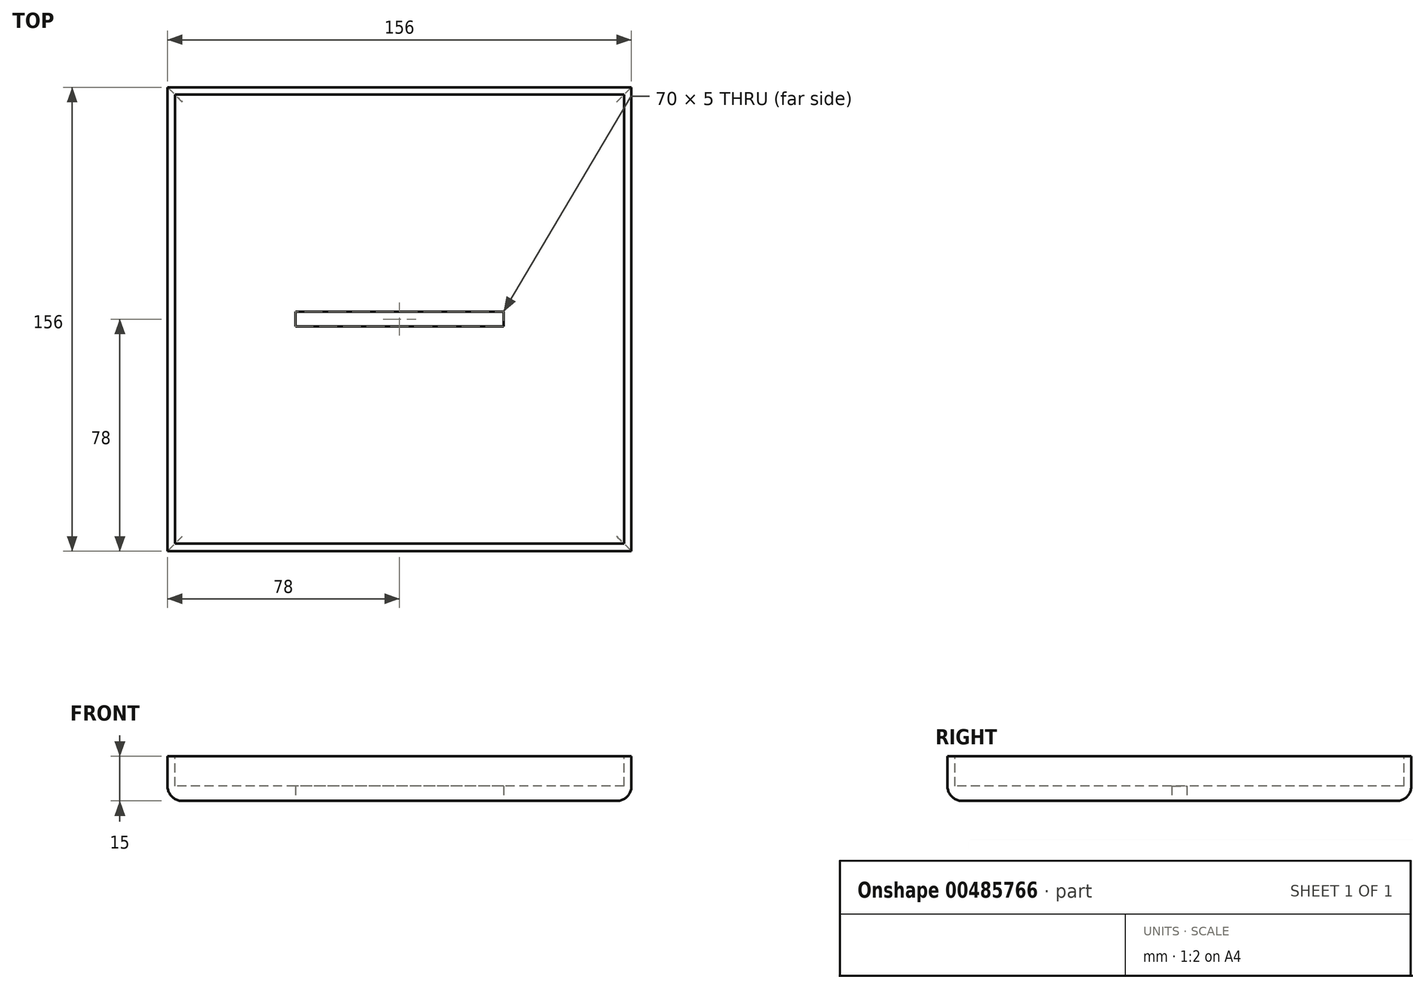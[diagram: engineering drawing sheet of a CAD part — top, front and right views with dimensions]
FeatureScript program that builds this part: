
annotation { "Feature Type Name" : "Feature", "Feature Type Description" : "" }
export const myFeature = defineFeature(function(context is Context, id is Id, definition is map)
    precondition{}
    {
        {
            var Q0;
            Q0=qCreatedBy(makeId("Top.planeOp"),FACE);
            var sketch = newSketch(context, id + "F0", { "sketchPlane" : qUnion([Q0])});
            skLineSegment(sketch, "E0.bottom", {"start": v(78, -78) * mm, "end": v(-78, -78) * mm});
            skLineSegment(sketch, "E0.top", {"start": v(78, 78) * mm, "end": v(-78, 78) * mm});
            skLineSegment(sketch, "E0.left", {"start": v(78, -78) * mm, "end": v(78, 78) * mm});
            skLineSegment(sketch, "E0.right", {"start": v(-78, -78) * mm, "end": v(-78, 78) * mm});
            skPoint(sketch, "E0.middle", {"position": v(0, 0) * mm});
            skSolve(sketch);
        }
        {
            var Q0;
            Q0 = qSketchRegion(id + "F0", true);
            extrude(context, id + "F1", {"entities" : qUnion([Q0]), "depth" : 15 * mm});
        }
        {
            var Q0;
            Q0=makeQuery(id+"F1.opExtrude","CAP_FACE",FACE,{"disambiguationData":[OSD([sQuery(id+"F0.wireOp",EDGE,"E0.bottom"),sQuery(id+"F0.wireOp",EDGE,"E0.top"),sQuery(id+"F0.wireOp",EDGE,"E0.left"),sQuery(id+"F0.wireOp",EDGE,"E0.right")])],"isStart":false});
            var sketch = newSketch(context, id + "F2", { "sketchPlane" : qUnion([Q0])});
            skLineSegment(sketch, "E1.bottom", {"start": v(75.5, 75.5) * mm, "end": v(-75.5, 75.5) * mm});
            skLineSegment(sketch, "E1.top", {"start": v(75.5, -75.5) * mm, "end": v(-75.5, -75.5) * mm});
            skLineSegment(sketch, "E1.left", {"start": v(75.5, 75.5) * mm, "end": v(75.5, -75.5) * mm});
            skLineSegment(sketch, "E1.right", {"start": v(-75.5, 75.5) * mm, "end": v(-75.5, -75.5) * mm});
            skPoint(sketch, "E1.middle", {"position": v(0, 0) * mm});
            skSolve(sketch);
        }
        {
            var Q0;
            Q0=makeQuery(id+"F2.imprint","IMPRINT",FACE,{"disambiguationData":[TD([[makeQuery(id+"F2.imprint","IMPRINT",EDGE,{"derivedFrom":sQuery(id+"F2.wireOp",EDGE,"E1.bottom")}),1.0]])]});
            extrude(context, id + "F3", {"entities" : qUnion([Q0]), "operationType" : NewBodyOperationType.REMOVE, "oppositeDirection" : true, "depth" : 10 * mm});
        }
        {
            var Q0;
            Q0=makeQuery(id+"F1.opExtrude","CAP_EDGE",EDGE,{"disambiguationData":[OSD([sQuery(id+"F0.wireOp",EDGE,"E0.left")])],"isStart":true});
            var Q1;
            Q1=makeQuery(id+"F1.opExtrude","CAP_EDGE",EDGE,{"disambiguationData":[OSD([sQuery(id+"F0.wireOp",EDGE,"E0.bottom")])],"isStart":true});
            var Q2;
            Q2=makeQuery(id+"F1.opExtrude","CAP_EDGE",EDGE,{"disambiguationData":[OSD([sQuery(id+"F0.wireOp",EDGE,"E0.right")])],"isStart":true});
            var Q3;
            Q3=makeQuery(id+"F1.opExtrude","CAP_EDGE",EDGE,{"disambiguationData":[OSD([sQuery(id+"F0.wireOp",EDGE,"E0.top")])],"isStart":true});
            fillet(context, id + "F4", {"entities" : qUnion([Q0, Q1, Q2, Q3]), "radius" : 5 * mm, "tangentPropagation" : true, "allowEdgeOverflow" : false});
        }
        {
            var Q0;
            Q0=makeQuery(id+"F1.opExtrude","CAP_FACE",FACE,{"disambiguationData":[OSD([sQuery(id+"F0.wireOp",EDGE,"E0.bottom"),sQuery(id+"F0.wireOp",EDGE,"E0.top"),sQuery(id+"F0.wireOp",EDGE,"E0.left"),sQuery(id+"F0.wireOp",EDGE,"E0.right")])],"isStart":true});
            var sketch = newSketch(context, id + "F5", { "sketchPlane" : qUnion([Q0])});
            skLineSegment(sketch, "E2.bottom", {"start": v(35, 2.5) * mm, "end": v(-35, 2.5) * mm});
            skLineSegment(sketch, "E2.top", {"start": v(35, -2.5) * mm, "end": v(-35, -2.5) * mm});
            skLineSegment(sketch, "E2.left", {"start": v(35, 2.5) * mm, "end": v(35, -2.5) * mm});
            skLineSegment(sketch, "E2.right", {"start": v(-35, 2.5) * mm, "end": v(-35, -2.5) * mm});
            skPoint(sketch, "E2.middle", {"position": v(0, 0) * mm});
            skSolve(sketch);
        }
        {
            var Q0;
            Q0=makeQuery(id+"F5.imprint","IMPRINT",FACE,{"disambiguationData":[TD([[makeQuery(id+"F5.imprint","IMPRINT",EDGE,{"derivedFrom":sQuery(id+"F5.wireOp",EDGE,"E2.bottom")}),1.0]])]});
            extrude(context, id + "F6", {"entities" : qUnion([Q0]), "operationType" : NewBodyOperationType.REMOVE, "oppositeDirection" : true, "depth" : 5 * mm});
        }
    });
